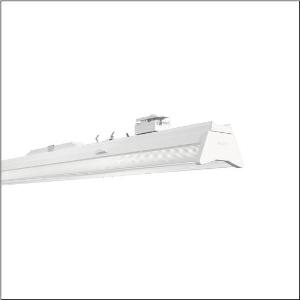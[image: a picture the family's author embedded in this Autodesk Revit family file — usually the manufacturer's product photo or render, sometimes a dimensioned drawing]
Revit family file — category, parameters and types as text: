
# Revit family: licross_11_performance_mo_51td16mn4axg
name_source: partatom
category: Lighting Fixtures
units: mm (PartAtom-declared; Revit-internal decimal feet)

## family parameters
Cut with Voids When Loaded = No
Host = Face
Light Source = No
Part Type = Normal
Room Calculation Point = No
Round Connector Dimension = Use Diameter
Shared = No

## types (1)
- --- (1 x LED, 10160 lm, 55.3 W, 4000K)
    Apparent Load = 55 VA
    CIE Flux Codes = 66 88 96 79 100
    Color Rendering = 80
    Color Temperature = 4000K
    Default Elevation = 1800 mm
    Description = Licross 11 Performance MO, luminaire insert, of sheet steel, galvanised, coil coated, white, length: 1.500mm, width: 120mm, height: 123mm, LED rated luminous flux: 10.160lm, light colour: 840, SDCM (Standard Deviation of Colour Matching)MacAdam ≤ 2 SDCM (initial), control gear: ON/OFF Multilumen, with plug, 3-pole, with phase selection, mains connection: 220..240V, AC, 50/60Hz, rated input power: 55W, internal wiring halogen-free, primary light control with lens, of plastic, primary optical cover: cover, of PMMA, light emission: direct/indirect distribution, primary light characteristic: symmetric, protection rating (complete): IP54, insulation class (complete): insulation class I (protective earthing), certification: CE, ENEC, VDE, UKCA, protection symbol: D if used in an environment with non-conductive dust loads with corresponding accessories, impact resistance: IK06, permissible ambient temperature for indoor applications: -35..+40°C, corresponds to IFS (International Featured Standards) requirements for safety and quality in the food industry, reducing of maximum allowable ambient temperature of 5°C with ceiling mounting, LABS conformity tested according to VDMA 24364:2018-05, The light source and the operating device comply with the requirements of the Ecodesign Regulation (EU) 2019/2020 and are replaceable in accordance with this regulation, packaging unit: 1 piece
    Height = 114 mm
    Lamp = 1 x LED
    Lamp Light Flux = 10160 lm
    Lamp Power = 55.3 W
    Lamp count = 1
    Length = 1500 mm
    Luminous efficacy = 184 lm/W
    Manufacturer = Siteco
    ModVariant = No
    Model = 51TD16MN4AXG
    Mounting Place = Ceiling
    Mounting Type = Pendant
    Number of Poles = 1
    OnlyDefault = Yes
    Power Factor = 1
    Product Name = Licross 11 Performance MO
    Product group = luminaire insert | ceiling pendant
    ProductGroupID = 901
    Protection Class = Protection class I
    Protection Degree = IP 54
    RLX_Detail_Level = 1
    RLX_Emergency_Light_Flux = 0 lm
    RLX_Emergency_Type = 0
    RLX_Emergency_Type_DB = No
    RlxData = <blob elided: 32109 chars, md5=36460c4d>
    Socket = socket
    Standby Power = 0 W
    System Light Flux = 10160 lm
    System Power = 55 W
    Type Comments = factory setting: luminous flux: 100 % | (A | C | E) | 126 mA
    Type Image = l_1256138.jpg
    URL = http://relux.com
    VarID = @adj_092113
    Voltage = 0 V
    Weight = 0.00 kg
    Width = 120 mm

## geometry (parser evidence)
native form markers: Blend x4, Sweep x10
no freeform markers — native parametric forms only
